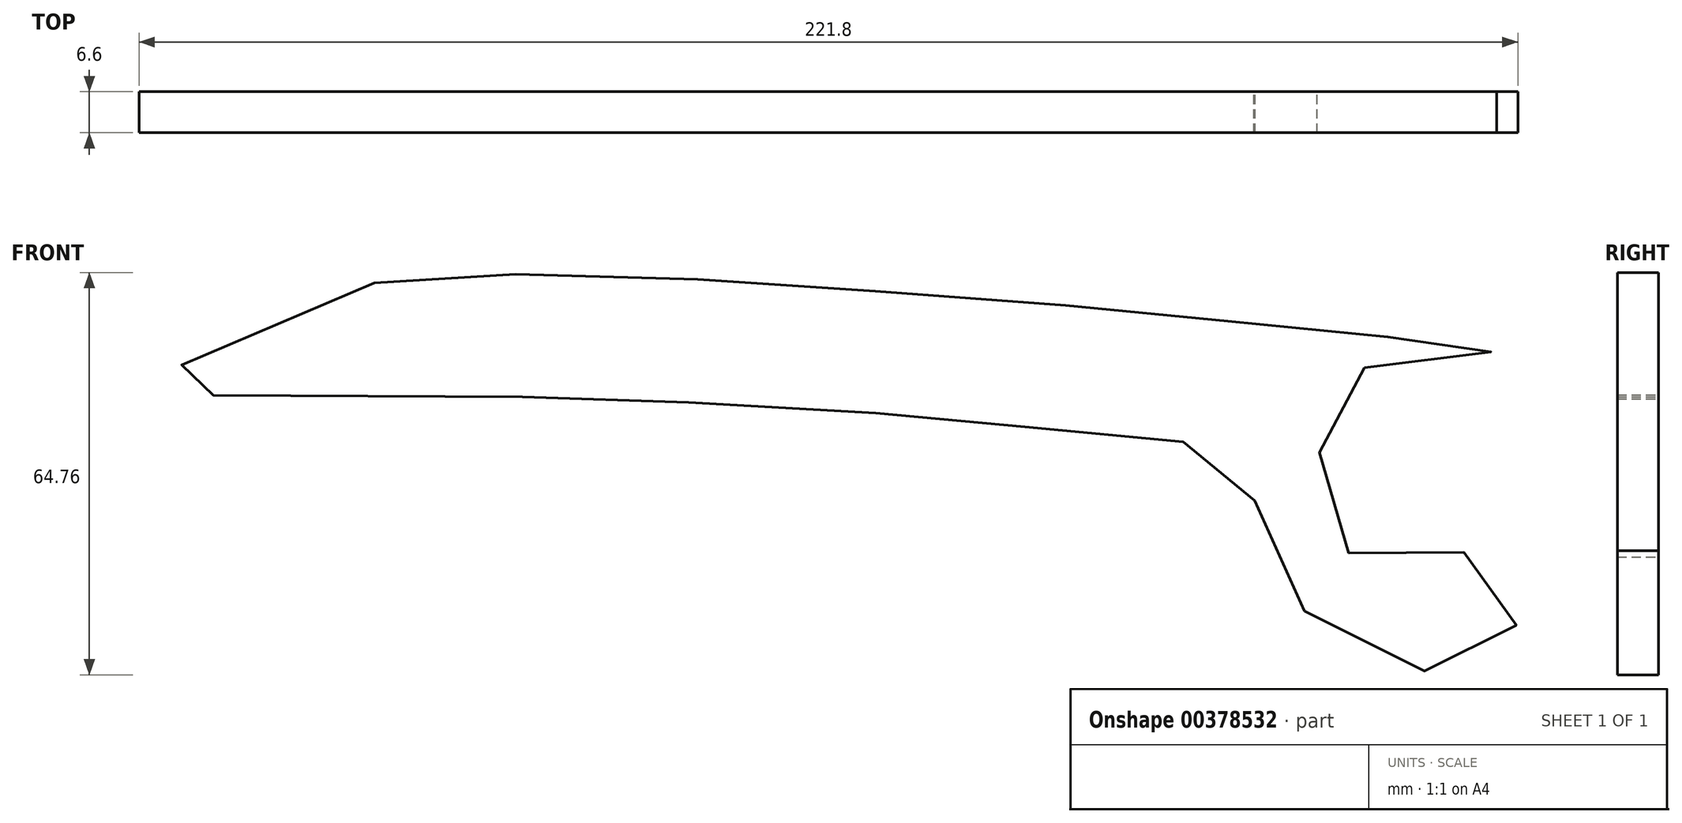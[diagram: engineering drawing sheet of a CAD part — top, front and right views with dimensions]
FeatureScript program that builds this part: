
annotation { "Feature Type Name" : "Feature", "Feature Type Description" : "" }
export const myFeature = defineFeature(function(context is Context, id is Id, definition is map)
    precondition{}
    {
        {
            var Q0;
            Q0=qCreatedBy(makeId("Front.planeOp"),FACE);
            var sketch = newSketch(context, id + "F0", { "sketchPlane" : qUnion([Q0])});
            skFitSpline(sketch, "E0", {"points": [v(94.23, -25.03) * mm, v(100.64, -28.4) * mm, v(102.86, -35.28) * mm, v(98.5, -43.25) * mm, v(88.33, -44.22) * mm, v(78.07, -39.85) * mm, v(64.57, -31.37) * mm, v(60.46, -22.24) * mm, v(59.94, -9.24) * mm, v(53.62, -7.52) * mm, v(31.72, -5.5) * mm, v(18.4, -4.36) * mm, v(0, -2.65) * mm, v(-7.06, -2.09) * mm, v(-50.66, 0) * mm, v(-54.64, 0) * mm, v(-114.75, 0) * mm, v(-118.88, 0) * mm, v(-103.18, 10.24) * mm, v(-75.31, 19.53) * mm, v(-62.8, 19.9) * mm, v(-37.96, 19.34) * mm, v(-16.74, 18.18) * mm, v(10.87, 16.21) * mm, v(36.2, 14.26) * mm, v(55.45, 12.3) * mm, v(73.73, 10.24) * mm, v(93.96, 8.76) * mm, v(99.5, 7.58) * mm, v(90.34, 6.62) * mm, v(78.56, 4.85) * mm, v(73.2, 0.4) * mm, v(71.15, -7.42) * mm, v(70.7, -16.51) * mm, v(74.7, -24.65) * mm, v(86.46, -25.2) * mm, v(94.23, -25.03) * mm]});
            skSolve(sketch);
        }
        {
            var Q0;
            Q0=makeQuery(id+"F0.imprint","IMPRINT",FACE,{"disambiguationData":[TD([[makeQuery(id+"F0.imprint","IMPRINT",EDGE,{"derivedFrom":sQuery(id+"F0.wireOp",EDGE,"E0")}),-1.0]])]});
            extrude(context, id + "F1", {"entities" : qUnion([Q0]), "depth" : 6.6 * mm});
        }
    });
